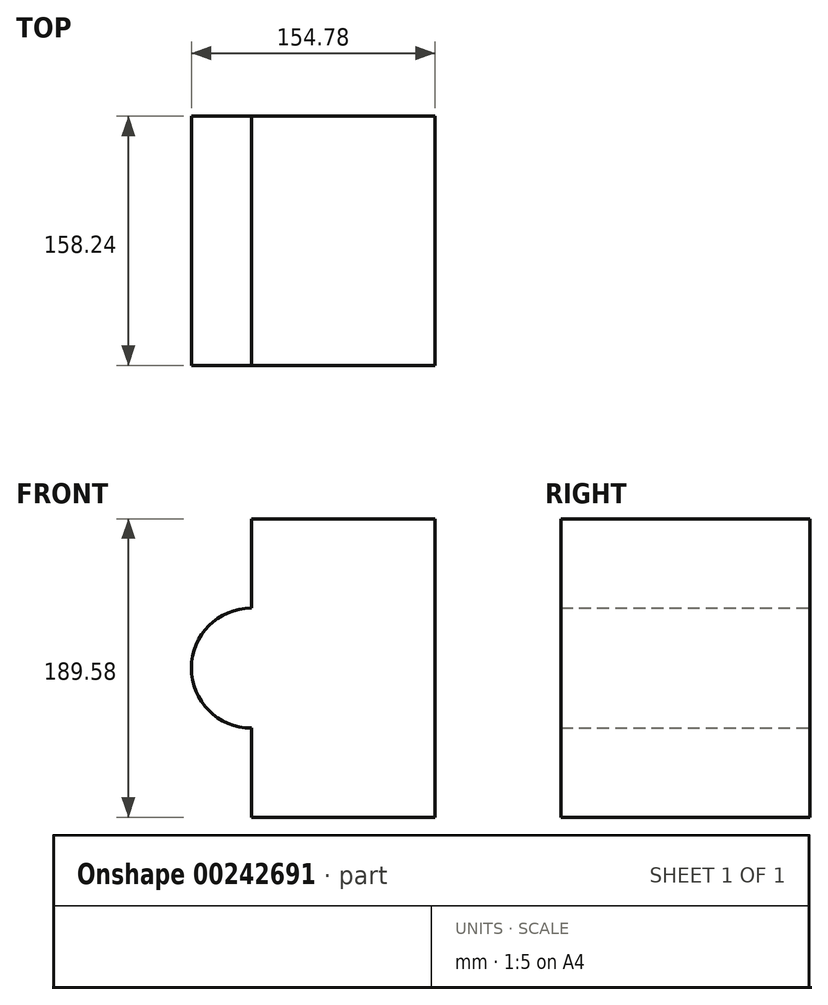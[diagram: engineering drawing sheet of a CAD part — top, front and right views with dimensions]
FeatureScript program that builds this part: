
annotation { "Feature Type Name" : "Feature", "Feature Type Description" : "" }
export const myFeature = defineFeature(function(context is Context, id is Id, definition is map)
    precondition{}
    {
        {
            var Q0;
            Q0=qCreatedBy(makeId("Front.planeOp"),FACE);
            var sketch = newSketch(context, id + "F0", { "sketchPlane" : qUnion([Q0])});
            skCircle(sketch, "E0", {"center": v(0, 0) * mm, "radius": 38.1 * mm});
            skSolve(sketch);
        }
        {
            var Q0;
            Q0=makeQuery(id+"F0.imprint","IMPRINT",FACE,{"disambiguationData":[TD([[makeQuery(id+"F0.imprint","IMPRINT",EDGE,{"derivedFrom":sQuery(id+"F0.wireOp",EDGE,"E0")}),1.0]])]});
            extrude(context, id + "F1", {"entities" : qUnion([Q0]), "depth" : 25.4 * mm});
        }
        {
            var Q0;
            Q0=qCreatedBy(makeId("Front.planeOp"),FACE);
            var sketch = newSketch(context, id + "F2", { "sketchPlane" : qUnion([Q0])});
            skArc(sketch, "E1.0", {"start": v(0, -38.1) * mm, "mid": v(38.1, 0) * mm, "end": v(0, 38.1) * mm});
            skLineSegment(sketch, "E2", {"start": v(0, 38.1) * mm, "end": v(0, 94.8) * mm});
            skLineSegment(sketch, "E3", {"start": v(0, 94.8) * mm, "end": v(116.68, 94.8) * mm});
            skLineSegment(sketch, "E4", {"start": v(116.68, 94.8) * mm, "end": v(116.68, 0) * mm});
            skLineSegment(sketch, "E5", {"start": v(116.68, 0) * mm, "end": v(0, 0) * mm, "construction": true});
            skLineSegment(sketch, "E6.MirrorCS", {"start": v(116.68, -94.8) * mm, "end": v(116.68, 0) * mm});
            skLineSegment(sketch, "E7.MirrorCS", {"start": v(0, -94.8) * mm, "end": v(116.68, -94.8) * mm});
            skLineSegment(sketch, "E8.MirrorCS", {"start": v(0, -38.1) * mm, "end": v(0, -94.8) * mm});
            skSolve(sketch);
        }
        {
            var Q0;
            Q0=makeQuery(id+"F2.imprint","IMPRINT",FACE,{"disambiguationData":[TD([[makeQuery(id+"F2.imprint","IMPRINT",EDGE,{"derivedFrom":sQuery(id+"F2.wireOp",EDGE,"E1.0")}),-1.0]])]});
            extrude(context, id + "F3", {"entities" : qUnion([Q0]), "depth" : 158.24 * mm});
        }
        {
            var Q0;
            Q0=makeQuery(id+"F1.opExtrude","CAP_FACE",FACE,{"disambiguationData":[OSD([sQuery(id+"F0.wireOp",EDGE,"E0")])],"isStart":false});
            var Q1;
            Q1=makeQuery(id+"F3.opExtrude","CAP_FACE",FACE,{"disambiguationData":[OSD([sQuery(id+"F2.wireOp",EDGE,"E1.0"),sQuery(id+"F2.wireOp",EDGE,"E2"),sQuery(id+"F2.wireOp",EDGE,"E3"),sQuery(id+"F2.wireOp",EDGE,"E4"),sQuery(id+"F2.wireOp",EDGE,"E6.MirrorCS"),sQuery(id+"F2.wireOp",EDGE,"E7.MirrorCS"),sQuery(id+"F2.wireOp",EDGE,"E8.MirrorCS")])],"isStart":false});
            extrude(context, id + "F4", {"entities" : qUnion([Q0]), "operationType" : NewBodyOperationType.ADD, "endBound" : BoundingType.UP_TO_SURFACE, "endBoundEntityFace" : qUnion([Q1]), "depth" : 25.4 * mm});
        }
    });
